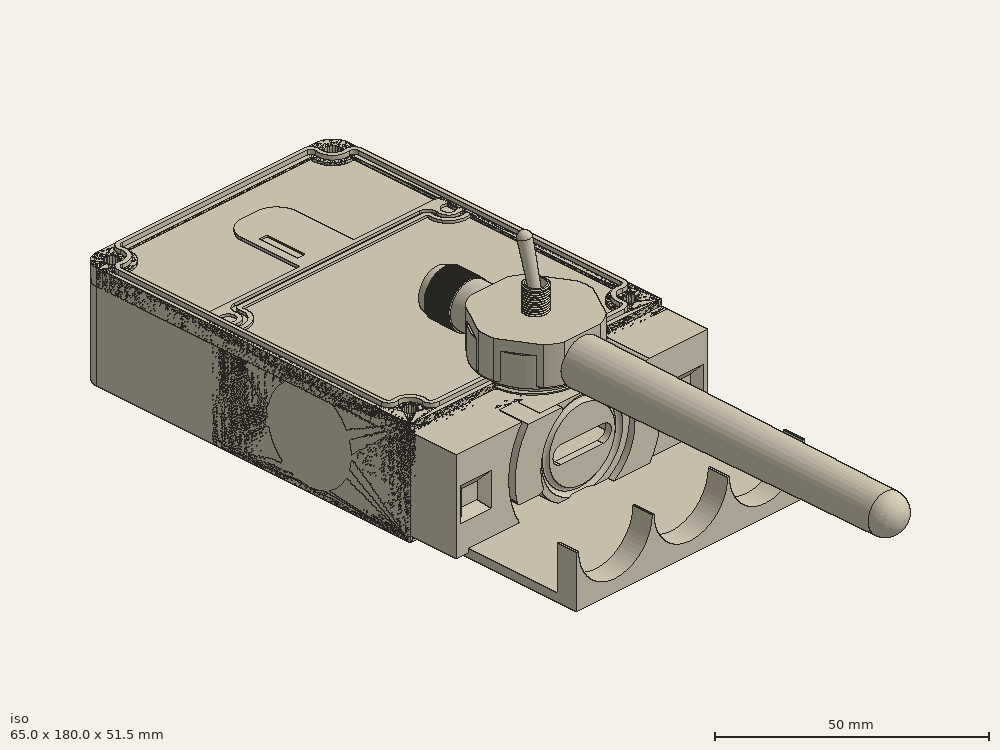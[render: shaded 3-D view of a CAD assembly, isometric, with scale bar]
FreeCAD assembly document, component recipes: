
FREECAD ASSEMBLY — COMPONENT RECIPES ("NomadShell_0.1")

This assembly document has 23 components, labeled P0..P22 below (a component is one placed body or linked part). 12 of them carry a construction recipe — the FreeCAD feature program that regenerates the part from scratch, quoted from this document or its linked companion documents; the rest are supplied as boundary geometry only. No exploded tour is included for this assembly.
NOTE — document 2 of 2 of this assembly tour. The two overview renders and the header above are repeated from document 1; the component sections below continue where the previous document stopped.
COMPONENT P12 — recipe-attached ("battery_top001", modeled in this document).
Construction recipe (the document's own serialized feature program — sketch geometry with constraints, then the solid features built on it; lengths are millimeters unless a unit is written):

FEATURE [PartDesign::SubShapeBinder] Binder005
  BindCopyOnChange = 0
  BindMode = 0
  ClaimChildren = false
  Context = -> Part009 [Body015.Binder005.]
  Fuse = false
  MakeFace = true
  OffsetFill = false
  OffsetIntersection = false
  OffsetJoinType = 0
  OffsetOpenResult = false
  PartialLoad = false
  Refine = true
  Relative = true
  Support = -> [Part002[Body002.Sketch007.]]
  _Version = 2
FEATURE [Sketcher::SketchObject] Sketch071  label="battery_holder"
  ArcFitTolerance = 1e-06
  AttachmentSupport = -> [XZ_Plane082]
  ExternalGeometry = -> [Binder005]
  ExternalTypes = [0,0,0,0,0,0,0,0,0,0,0]
  FullyConstrained = true
  MakeInternals = false
  MapMode = 5
  Placement = pos=(0,0,0) rot=(1,0,0;1.5708rad)
  sketch-geometry (3):
    g0: LineSegment StartX=-29.4 StartY=-12 StartZ=0 EndX=-29.4 EndY=-24.5 EndZ=0
    g1: LineSegment StartX=-29.4 StartY=-24.5 StartZ=0 EndX=29.5 EndY=-24.5 EndZ=0
    g2: LineSegment StartX=29.5 StartY=-24.5 StartZ=0 EndX=29.5 EndY=-12 EndZ=0
  constraints (8):
    c: Coincident(g-4,g0)
    c: Vertical(g0)
    c: Coincident(g0,g1)
    c: Horizontal(g1)
    c: Coincident(g1,g2)
    c: Coincident(g2,g-10)
    c: Parallel(g2,g-2)
    c: Distance(g-5,g1) = 3
FEATURE [PartDesign::Pad] Pad026  label="battery_holder001"
  Direction = (0,-1,2e-16)
  Length = 5
  Length2 = 10
  Placement = pos=(0,0,0) rot=(1,0,0;1.5708rad)
  Profile = -> Sketch071 [Edge2,Edge3,Vertex4,Edge4,Edge5,Edge6,Edge7,Edge8,Edge9,Edge10,Edge1]
  ReferenceAxis = -> Sketch071 [N_Axis]
  Refine = true
  Suppressed = false
  Type = 0
FEATURE [Sketcher::SketchObject] Sketch072
  ArcFitTolerance = 1e-06
  AttachmentSupport = -> [XZ_Plane082]
  ExternalGeometry = -> [Sketch071]
  ExternalTypes = [0]
  FullyConstrained = true
  MakeInternals = false
  MapMode = 5
  Placement = pos=(0,0,0) rot=(1,0,0;1.5708rad)
  sketch-geometry (3):
    g0: LineSegment StartX=-29.4 StartY=-24.5 StartZ=0 EndX=-29.4 EndY=-22.5 EndZ=0
    g1: LineSegment StartX=-29.4 StartY=-22.5 StartZ=0 EndX=29.5 EndY=-22.5 EndZ=0
    g2: LineSegment StartX=29.5 StartY=-22.5 StartZ=0 EndX=29.5 EndY=-24.5 EndZ=0
  constraints (8):
    c: Coincident(g0,g-3)
    c: Coincident(g0,g1)
    c: Horizontal(g1)
    c: Coincident(g1,g2)
    c: Coincident(g2,g-3)
    c: Parallel(g2,g-2)
    c: Parallel(g0,g-2)
    c: Distance(g0,g0) = 2
FEATURE [PartDesign::Pad] Pad027
  BaseFeature = -> Pad026
  Direction = (0,-1,2e-16)
  Length = 20
  Length2 = 10
  Placement = pos=(0,0,0) rot=(1,0,0;1.5708rad)
  Profile = -> Sketch072
  ReferenceAxis = -> Sketch072 [N_Axis]
  Refine = true
  Suppressed = false
  Type = 0
FEATURE [PartDesign::Mirrored] Mirrored
  BaseFeature = -> Pad027
  MirrorPlane = -> Pad027 [Face1]
  Originals = -> [Pad027]
  Placement = pos=(0,0,0) rot=(1,0,0;1.5708rad)
  Refine = true
  Suppressed = false
  TransformMode = 1
FEATURE [PartDesign::Body] Body015  label="Body"
  AllowCompound = false
  Group = -> [Binder005,Sketch071,Pad026,Sketch072,Pad027,Mirrored]
  Origin = -> Origin165
  Tip = -> Mirrored
COMPONENT P13 — recipe-attached ("gasket_main_body003", modeled in this document).
Construction recipe (the document's own serialized feature program — sketch geometry with constraints, then the solid features built on it; lengths are millimeters unless a unit is written):

FEATURE [PartDesign::SubShapeBinder] Binder
  BindCopyOnChange = 0
  BindMode = 0
  ClaimChildren = false
  Context = -> Body001 [Binder.]
  Fuse = false
  MakeFace = true
  OffsetFill = false
  OffsetIntersection = false
  OffsetJoinType = 0
  OffsetOpenResult = false
  PartialLoad = false
  Refine = true
  Relative = true
  Support = -> [Part[Body.Sketch.]]
  _Version = 2
FEATURE [Sketcher::SketchObject] Sketch027  label="center_line"
  ArcFitTolerance = 1e-06
  AttachmentSupport = -> [XY_Plane055]
  ExternalGeometry = -> [Binder]
  ExternalTypes = [0,0,0,0,0,0,0,0,0,0,0,0,0,0,0,0]
  FullyConstrained = true
  MakeInternals = false
  MapMode = 5
FEATURE [Sketcher::SketchObject] Sketch069  label="profile"
  ArcFitTolerance = 1e-06
  AttachmentSupport = -> [YZ_Plane055]
  ExternalGeometry = -> [Sketch027]
  ExternalTypes = [0]
  FullyConstrained = true
  MakeInternals = false
  MapMode = 5
  Placement = pos=(0,0,0) rot=(0.57735,0.57735,0.57735;2.0944rad)
  expr: Constraints[10] = VarSet.Base_gasket_width
  expr: Constraints[11] = VarSet.Base_gasket_height
  sketch-geometry (5):
    g0: LineSegment StartX=1 StartY=1 StartZ=0 EndX=1 EndY=-1 EndZ=0
    g1: LineSegment StartX=1 StartY=-1 StartZ=0 EndX=2 EndY=-1 EndZ=0
    g2: LineSegment StartX=2 StartY=-1 StartZ=0 EndX=2 EndY=1 EndZ=0
    g3: LineSegment StartX=2 StartY=1 StartZ=0 EndX=1 EndY=1 EndZ=0
    g4: GeomPoint [constr] X=1.5 Y=0 Z=0
  constraints (12):
    c: Coincident(g0,g1)
    c: Coincident(g1,g2)
    c: Coincident(g2,g3)
    c: Coincident(g3,g0)
    c: Vertical(g0)
    c: Vertical(g2)
    c: Horizontal(g1)
    c: Horizontal(g3)
    c: Symmetric(g2,g0,g4)
    c: Coincident(g4,g-3)
    c: Distance(g3,g3) = 1
    c: DistanceY(g0,g0) = 2
FEATURE [PartDesign::AdditivePipe] AdditivePipe
  AuxilleryCurvelinear = true
  AuxillerySpineTangent = false
  Binormal = (0,0,0)
  Mode = 0
  Placement = pos=(0,0,0) rot=(1,1,1;2.0944rad)
  Profile = -> Sketch069
  Refine = true
  Spine = -> Sketch027 [Edge1,Edge16,Edge15,Edge14,Edge13,Edge12,Edge11,Edge10,Edge9,Edge8,Edge7,Edge6,Edge5,Edge4,Edge3,Edge2]
  SpineTangent = false
  Suppressed = false
  Transformation = 0
  Transition = 0
FEATURE [PartDesign::Body] Body001  label="gasket_main_body001"
  AllowCompound = false
  Group = -> [Binder,Sketch027,Sketch069,AdditivePipe]
  Origin = -> Origin110
  Tip = -> AdditivePipe
COMPONENT P14 — recipe-attached ("gps_antenna002", modeled in this document).
Construction recipe (the document's own serialized feature program — sketch geometry with constraints, then the solid features built on it; lengths are millimeters unless a unit is written):

FEATURE [Sketcher::SketchObject] Sketch042
  ArcFitTolerance = 1e-06
  AttachmentSupport = -> [XY_Plane077]
  ExternalTypes = [0]
  FullyConstrained = true
  MakeInternals = false
  MapMode = 5
  expr: Constraints[10] = VarSet.Base_gps_antenna_width
  expr: Constraints[11] = VarSet.Base_gps_antenna_lenght
  sketch-geometry (15):
    g0: LineSegment StartX=-7.5 StartY=7.5 StartZ=0 EndX=-7.5 EndY=-7.5 EndZ=0
    g1: LineSegment StartX=-7.5 StartY=-7.5 StartZ=0 EndX=7.5 EndY=-7.5 EndZ=0
    g2: LineSegment StartX=7.5 StartY=-7.5 StartZ=0 EndX=7.5 EndY=7.5 EndZ=0
    g3: LineSegment StartX=7.5 StartY=7.5 StartZ=0 EndX=-7.5 EndY=7.5 EndZ=0
    g4: GeomPoint [constr] X=0 Y=0 Z=0
    g5: LineSegment StartX=-6.5 StartY=-6.5 StartZ=0 EndX=6.5 EndY=-6.5 EndZ=0
    g6: LineSegment StartX=6.5 StartY=-6.5 StartZ=0 EndX=6.5 EndY=6.5 EndZ=0
    g7: LineSegment StartX=6.5 StartY=6.5 StartZ=0 EndX=-6.5 EndY=6.5 EndZ=0
    g8: LineSegment StartX=-6.5 StartY=6.5 StartZ=0 EndX=-6.5 EndY=-6.5 EndZ=0
    g9: GeomPoint [constr] X=0 Y=0 Z=0
    g10: LineSegment StartX=-6 StartY=-6 StartZ=0 EndX=6 EndY=-6 EndZ=0
    g11: LineSegment StartX=6 StartY=-6 StartZ=0 EndX=6 EndY=6 EndZ=0
    g12: LineSegment StartX=6 StartY=6 StartZ=0 EndX=-6 EndY=6 EndZ=0
    g13: LineSegment StartX=-6 StartY=6 StartZ=0 EndX=-6 EndY=-6 EndZ=0
    g14: GeomPoint [constr] X=0 Y=0 Z=0
  constraints (36):
    c: Coincident(g0,g1)
    c: Coincident(g1,g2)
    c: Coincident(g2,g3)
    c: Coincident(g3,g0)
    c: Vertical(g0)
    c: Vertical(g2)
    c: Horizontal(g1)
    c: Horizontal(g3)
    c: Symmetric(g2,g0,g4)
    c: Coincident(g4,g-1)
    c: DistanceX(g0,g2) = 15
    c: DistanceY(g0,g0) = 15
    c: Coincident(g5,g6)
    c: Coincident(g6,g7)
    c: Coincident(g7,g8)
    c: Coincident(g8,g5)
    c: Horizontal(g5)
    c: Horizontal(g7)
    c: Vertical(g6)
    c: Vertical(g8)
    c: Symmetric(g7,g5,g9)
    c: Distance(g6,g8) = 13
    c: Distance(g5,g7) = 13
    c: Coincident(g9,g4)
    c: Coincident(g10,g11)
    c: Coincident(g11,g12)
    c: Coincident(g12,g13)
    c: Coincident(g13,g10)
    c: Horizontal(g10)
    c: Horizontal(g12)
    c: Vertical(g11)
    c: Vertical(g13)
    c: Symmetric(g12,g10,g14)
    c: Distance(g11,g13) = 12
    c: Distance(g10,g12) = 12
    c: Coincident(g14,g4)
FEATURE [PartDesign::Pad] Pad015
  Direction = (0,0,1)
  Length = 0.6
  Length2 = 10
  Profile = -> Sketch042 [Edge4,Edge3,Edge2,Edge1]
  ReferenceAxis = -> Sketch042 [N_Axis]
  Refine = true
  Suppressed = false
  Type = 0
FEATURE [PartDesign::Pad] Pad016
  BaseFeature = -> Pad015
  Direction = (0,0,1)
  Length = 5
  Length2 = 10
  Profile = -> Sketch042 [Edge5,Edge8,Edge7,Edge6]
  ReferenceAxis = -> Sketch042 [N_Axis]
  Refine = true
  Suppressed = false
  Type = 0
FEATURE [PartDesign::Pad] Pad017
  BaseFeature = -> Pad016
  Direction = (0,0,1)
  Length = 1.3
  Length2 = 10
  Profile = -> Sketch042 [Edge12,Edge9,Edge10,Edge11]
  ReferenceAxis = -> Sketch042 [N_Axis]
  Refine = true
  Reversed = true
  Suppressed = false
  Type = 0
FEATURE [Sketcher::SketchObject] Sketch044
  ArcFitTolerance = 1e-06
  ExternalTypes = [0]
  FullyConstrained = true
  MakeInternals = false
  MapMode = 5
  Placement = pos=(0,0,5) rot=(0,0,1;0rad)
  sketch-geometry (1):
    g0: Circle CenterX=0 CenterY=1.5 CenterZ=0 NormalX=0 NormalY=0 NormalZ=1 AngleXU=0 Radius=1
  constraints (3):
    c: PointOnObject(g0,g-2)
    c: Diameter(g0) = 2
    c: DistanceY(g-1,g0) = 1.5
FEATURE [PartDesign::Pad] Pad018
  BaseFeature = -> Pad017
  Direction = (0,0,1)
  Length = 1
  Length2 = 10
  Profile = -> Sketch044
  ReferenceAxis = -> Sketch044 [N_Axis]
  Refine = true
  Suppressed = false
  Type = 0
FEATURE [PartDesign::Chamfer] Chamfer
  Angle = 45
  Base = -> Pad018 [Edge21,Edge24,Edge26,Vertex18,Edge22]
  BaseFeature = -> Pad018
  ChamferType = 0
  FlipDirection = false
  Refine = true
  Size = 2
  Size2 = 1
  SupportTransform = false
  Suppressed = false
  UseAllEdges = false
FEATURE [Sketcher::SketchObject] Sketch045
  ArcFitTolerance = 1e-06
  AttachmentSupport = -> [Chamfer]
  ExternalTypes = [0]
  FullyConstrained = true
  MakeInternals = false
  MapMode = 5
  Placement = pos=(0,6,0) rot=(0,0.707107,0.707107;3.14159rad)
  sketch-geometry (1):
    g0: Circle CenterX=0 CenterY=-0.7 CenterZ=0 NormalX=0 NormalY=0 NormalZ=1 AngleXU=0 Radius=0.5
  constraints (3):
    c: PointOnObject(g0,g-2)
    c: Diameter(g0) = 1
    c: Distance(g0,g-1) = 0.7
FEATURE [PartDesign::Pad] Pad019
  BaseFeature = -> Chamfer
  Direction = (0,1,-2e-16)
  Length = 5
  Length2 = 10
  Profile = -> Sketch045
  ReferenceAxis = -> Sketch045 [N_Axis]
  Refine = true
  Suppressed = false
  Type = 0
FEATURE [PartDesign::Body] Body012  label="gps_antenna001"
  AllowCompound = false
  Group = -> [Sketch042,Pad015,Pad016,Pad017,Sketch044,Pad018,Chamfer,Sketch045,Pad019]
  Origin = -> Origin155
  Tip = -> Pad019
COMPONENT P15 — recipe-attached ("mainbody_cover002", modeled in this document).
Construction recipe (the document's own serialized feature program — sketch geometry with constraints, then the solid features built on it; lengths are millimeters unless a unit is written):

FEATURE [Sketcher::SketchObject] Sketch025
  ArcFitTolerance = 1e-06
  AttachmentSupport = -> [XY_Plane070]
  ExternalTypes = [0]
  FullyConstrained = true
  MakeInternals = false
  MapMode = 5
  expr: Constraints[7] = VarSet.base_width
  expr: Constraints[8] = VarSet.Base_base_lenght
  sketch-geometry (8):
    g0: LineSegment StartX=-32.5 StartY=51 StartZ=0 EndX=-32.5 EndY=0 EndZ=0
    g1: LineSegment StartX=-32.5 StartY=0 StartZ=0 EndX=32.5 EndY=0 EndZ=0
    g2: LineSegment StartX=32.5 StartY=0 StartZ=0 EndX=32.5 EndY=51 EndZ=0
    g3: LineSegment StartX=28.5 StartY=55 StartZ=0 EndX=-28.5 EndY=55 EndZ=0
    g4: ArcOfCircle CenterX=-28.5 CenterY=51 CenterZ=0 NormalX=0 NormalY=0 NormalZ=1 AngleXU=0 Radius=4 StartAngle=1.5708 EndAngle=3.14159
    g5: GeomPoint [constr] X=-32.5 Y=55 Z=0
    g6: ArcOfCircle CenterX=28.5 CenterY=51 CenterZ=0 NormalX=0 NormalY=0 NormalZ=1 AngleXU=0 Radius=4 StartAngle=4.17e-14 EndAngle=1.5708
    g7: GeomPoint [constr] X=32.5 Y=55 Z=0
  constraints (19):
    c: Coincident(g0,g1)
    c: Coincident(g1,g2)
    c: Vertical(g0)
    c: Vertical(g2)
    c: Horizontal(g1)
    c: PointOnObject(g1,g-1)
    c: Symmetric(g5,g7,g-2)
    c: DistanceX(g5,g7) = 65
    c: DistanceY(g1,g7) = 55
    c: PointOnObject(g5,g0)
    c: PointOnObject(g5,g3)
    c: Tangent(g0,g4) = -1.5708
    c: Tangent(g3,g4) = -1.5708
    c: PointOnObject(g7,g2)
    c: PointOnObject(g7,g3)
    c: Tangent(g2,g6) = -1.5708
    c: Tangent(g3,g6) = -1.5708
    c: Equal(g4,g6)
    c: Radius(g4) = 4
FEATURE [PartDesign::SubShapeBinder] Binder001
  BindCopyOnChange = 0
  BindMode = 0
  ClaimChildren = false
  Context = -> Body007 [Binder001.]
  Fuse = false
  MakeFace = true
  OffsetFill = false
  OffsetIntersection = false
  OffsetJoinType = 0
  OffsetOpenResult = false
  PartialLoad = false
  Refine = true
  Relative = true
  Support = -> [Part[Body.Sketch.]]
  _Version = 2
FEATURE [PartDesign::Pad] Pad011
  Direction = (0,0,1)
  Length = 5
  Length2 = 10
  Profile = -> Sketch025
  ReferenceAxis = -> Sketch025 [N_Axis]
  Refine = true
  Suppressed = false
  Type = 0
  expr: Length = VarSet.Base_lid_thickness
FEATURE [Sketcher::SketchObject] Sketch026
  ArcFitTolerance = 1e-06
  AttachmentSupport = -> [Pad011]
  ExternalGeometry = -> [Binder001]
  ExternalTypes = [0,0,0,0]
  FullyConstrained = false
  MakeInternals = false
  MapMode = 5
  Placement = pos=(0,0,5) rot=(0,0,1;0rad)
  sketch-geometry (4):
    g0: Circle CenterX=-28.5 CenterY=51 CenterZ=0 NormalX=0 NormalY=0 NormalZ=1 AngleXU=0 Radius=3.19333
    g1: Circle CenterX=28.5 CenterY=51 CenterZ=0 NormalX=0 NormalY=0 NormalZ=1 AngleXU=0 Radius=3.19333
    g2: Circle CenterX=28.5 CenterY=4 CenterZ=0 NormalX=0 NormalY=0 NormalZ=1 AngleXU=0 Radius=3.19333
    g3: Circle CenterX=-28.5 CenterY=4 CenterZ=0 NormalX=0 NormalY=0 NormalZ=1 AngleXU=0 Radius=3.19333
  constraints (7):
    c: Coincident(g0,g-3)
    c: Coincident(g1,g-4)
    c: Coincident(g2,g-5)
    c: Coincident(g3,g-6)
    c: Equal(g3,g2)
    c: Equal(g2,g1)
    c: Equal(g1,g0)
FEATURE [PartDesign::Hole] Hole
  BaseFeature = -> Pad011
  CustomThreadClearance = 0
  Depth = 25
  DepthType = 0
  Diameter = 3.4
  DrillForDepth = false
  DrillPoint = 1
  DrillPointAngle = 118
  HoleCutCountersinkAngle = 90
  HoleCutCustomValues = false
  HoleCutDepth = 0
  HoleCutDiameter = 6.7
  HoleCutType = 2
  ModelThread = false
  Profile = -> Sketch026
  Refine = true
  Suppressed = false
  Tapered = false
  TaperedAngle = 90
  ThreadClass = 0
  ThreadDepth = 25
  ThreadDepthType = 0
  ThreadDirection = 0
  ThreadFit = 0
  ThreadSize = 9
  ThreadType = 1
  Threaded = false
  UseCustomThreadClearance = false
FEATURE [Sketcher::SketchObject] Sketch034  label="gasket"
  ArcFitTolerance = 1e-06
  AttachmentSupport = -> [XY_Plane070]
  ExternalGeometry = -> [Binder001]
  ExternalTypes = [0,0,0,0,0,0,0,0,0,0,0,0,0,0,0,0,0]
  FullyConstrained = true
  MakeInternals = false
  MapMode = 5
FEATURE [Sketcher::SketchObject] Sketch035
  ArcFitTolerance = 1e-06
  AttachmentSupport = -> [YZ_Plane070]
  ExternalGeometry = -> [Sketch034]
  ExternalTypes = [0]
  FullyConstrained = true
  MakeInternals = false
  MapMode = 5
  Placement = pos=(0,0,0) rot=(0.57735,0.57735,0.57735;2.0944rad)
  expr: Constraints[10] = VarSet.Base_gasket_width
  expr: Constraints[11] = VarSet.Base_gasket_height
  sketch-geometry (5):
    g0: LineSegment StartX=1 StartY=1 StartZ=0 EndX=1 EndY=-1 EndZ=0
    g1: LineSegment StartX=1 StartY=-1 StartZ=0 EndX=2 EndY=-1 EndZ=0
    g2: LineSegment StartX=2 StartY=-1 StartZ=0 EndX=2 EndY=1 EndZ=0
    g3: LineSegment StartX=2 StartY=1 StartZ=0 EndX=1 EndY=1 EndZ=0
    g4: GeomPoint [constr] X=1.5 Y=0 Z=0
  constraints (12):
    c: Coincident(g0,g1)
    c: Coincident(g1,g2)
    c: Coincident(g2,g3)
    c: Coincident(g3,g0)
    c: Vertical(g0)
    c: Vertical(g2)
    c: Horizontal(g1)
    c: Horizontal(g3)
    c: Symmetric(g2,g0,g4)
    c: Coincident(g4,g-3)
    c: DistanceX(g0,g2) = 1
    c: DistanceY(g0,g0) = 2
FEATURE [PartDesign::SubtractivePipe] SubtractivePipe002
  AuxilleryCurvelinear = true
  AuxillerySpineTangent = false
  BaseFeature = -> Hole
  Binormal = (0,0,0)
  Mode = 0
  Profile = -> Sketch035
  Refine = true
  Spine = -> Sketch034 [Edge13,Edge14,Edge15,Edge16,Edge1,Edge2,Edge3,Edge4,Edge5,Edge6,Edge7,Edge8,Edge9,Edge10,Edge11,Edge12]
  SpineTangent = false
  Suppressed = false
  Transformation = 0
  Transition = 0
FEATURE [Sketcher::SketchObject] Sketch067  label="seses"
  ArcFitTolerance = 1e-06
  AttachmentSupport = -> [XY_Plane070]
  ExternalGeometry = -> [Binder001]
  ExternalTypes = [0,0,0,0,0,0,0,0]
  FullyConstrained = true
  MakeInternals = false
  MapMode = 5
FEATURE [PartDesign::Pocket] Pocket034
  BaseFeature = -> SubtractivePipe002
  Direction = (0,0,-1)
  Length = 0.6
  Length2 = 5
  Profile = -> Sketch067
  ReferenceAxis = -> Sketch067 [N_Axis]
  Refine = true
  Reversed = true
  Suppressed = false
  Type = 0
  expr: Length = 0.2 * VarSet.Base_case_thickness
FEATURE [PartDesign::Fillet] Fillet005
  Base = -> Pocket034 [Edge4,Edge7,Edge34,Edge35,Edge10,Edge36]
  BaseFeature = -> Pocket034
  Radius = 1
  Refine = true
  SupportTransform = false
  Suppressed = false
  UseAllEdges = false
FEATURE [PartDesign::Body] Body007  label="mainbody_cover001"
  AllowCompound = false
  Group = -> [Sketch025,Binder001,Pad011,Sketch026,Hole,Sketch034,Sketch035,SubtractivePipe002,Sketch067,Pocket034,Fillet005]
  Origin = -> Origin141
  Tip = -> Fillet005
COMPONENT P16 — geometry summary ("on_off_switch002"; no construction recipe available for this part):
  bounding box: 30.5 x 13.0 x 7.9 mm
  tessellated surface: 29,670 triangles
  volume: 1114 mm^3 (36% of its bounding box)
  symmetry: mirror-symmetric across its z mid-plane
COMPONENT P17 — recipe-attached ("oring002", modeled in this document).
Construction recipe (the document's own serialized feature program — sketch geometry with constraints, then the solid features built on it; lengths are millimeters unless a unit is written):

FEATURE [Sketcher::SketchObject] Sketch055
  ArcFitTolerance = 1e-06
  AttachmentSupport = -> [XY_Plane079]
  ExternalTypes = [0]
  FullyConstrained = false
  MakeInternals = false
  MapMode = 5
  expr: Constraints[0] = VarSet.Base_connector_oring_cross_section
  expr: Constraints[1] = (VarSet.Base_connector_oring_outside_diameter - VarSet.Base_connector_oring_cross_section) / 2
  expr: Constraints[4] = VarSet.Base_connector_oring_outside_diameter / 2
  sketch-geometry (2):
    g0: Circle CenterX=9.5 CenterY=0 CenterZ=0 NormalX=0 NormalY=0 NormalZ=1 AngleXU=0 Radius=1
    g1: LineSegment [constr] StartX=0 StartY=0 StartZ=0 EndX=10.5 EndY=0 EndZ=0
  constraints (5):
    c: Diameter(g0) = 2
    c: DistanceX(g-1,g0) = 9.5
    c: Coincident(g1,g-1)
    c: PointOnObject(g1,g-1)
    c: DistanceX(g1,g1) = 10.5
FEATURE [PartDesign::Revolution] Revolution002
  Angle = 360
  Angle2 = 60
  Axis = (0,1,0)
  Base = (0,0,0)
  Profile = -> Sketch055
  ReferenceAxis = -> Sketch055 [V_Axis]
  Refine = true
  Reversed = true
  Suppressed = false
  Type = 0
FEATURE [PartDesign::Body] Body013  label="oring001"
  AllowCompound = false
  Group = -> [Sketch055,Revolution002]
  Origin = -> Origin159
  Tip = -> Revolution002
COMPONENT P18 — geometry summary ("switch_cover001"; no construction recipe available for this part):
  bounding box: 17.0 x 10.9 x 9.7 mm
  tessellated surface: 23,872 triangles
  volume: 364 mm^3 (20% of its bounding box)
  symmetry: 6-fold rotationally symmetric about the y axis; mirror-symmetric across its x mid-plane
COMPONENT P19 — geometry summary ("usb_c_male001"; no construction recipe available for this part):
  bounding box: 38.4 x 11.8 x 6.9 mm
  tessellated surface: 6,336 triangles
  volume: 1915 mm^3 (61% of its bounding box)
  symmetry: 2-fold rotationally symmetric about the x axis; mirror-symmetric across its z mid-plane
COMPONENT P20 — recipe-attached ("usb_cover_base001", modeled in this document).
Construction recipe (the document's own serialized feature program — sketch geometry with constraints, then the solid features built on it; lengths are millimeters unless a unit is written):

FEATURE [Sketcher::SketchObject] Sketch008  label="main_usb_cover"
  ArcFitTolerance = 1e-06
  AttachmentSupport = -> [XZ_Plane063]
  ExternalTypes = [0]
  FullyConstrained = true
  MakeInternals = false
  MapMode = 5
  Placement = pos=(0,0,0) rot=(1,0,0;1.5708rad)
  expr: Constraints[12] = VarSet.Base_case_thickness / 2
  expr: Constraints[14] = VarSet.Base_usb_cover_main_diameter * 1.2 / 2
  expr: Constraints[15] = VarSet.Base_usb_cover_main_diameter / 2
  sketch-geometry (6):
    g0: LineSegment StartX=-9 StartY=0 StartZ=0 EndX=-10.8 EndY=0 EndZ=0
    g1: LineSegment StartX=-10.8 StartY=0 StartZ=0 EndX=-10.8 EndY=1.5 EndZ=0
    g2: LineSegment StartX=-10.8 StartY=1.5 StartZ=0 EndX=-10.4 EndY=1.5 EndZ=0
    g3: LineSegment StartX=-10.4 StartY=1.5 StartZ=0 EndX=-10.4 EndY=7.5 EndZ=0
    g4: LineSegment StartX=-10.4 StartY=7.5 StartZ=0 EndX=-9 EndY=7.5 EndZ=0
    g5: LineSegment StartX=-9 StartY=7.5 StartZ=0 EndX=-9 EndY=0 EndZ=0
  constraints (18):
    c: PointOnObject(g0,g-1)
    c: PointOnObject(g0,g-1)
    c: Coincident(g0,g1)
    c: Coincident(g1,g2)
    c: Horizontal(g2)
    c: Coincident(g2,g3)
    c: Coincident(g3,g4)
    c: Coincident(g4,g5)
    c: Coincident(g5,g0)
    c: Parallel(g5,g-2)
    c: Parallel(g4,g-1)
    c: Parallel(g1,g-2)
    c: DistanceY(g0,g1) = 1.5
    c: Parallel(g3,g5)
    c: DistanceX(g0,g-1) = 10.8
    c: DistanceX(g0,g-1) = 9
    c: DistanceY(g2,g3) = 6
    c: Distance(g4,g4) = 1.4
FEATURE [PartDesign::Revolution] Revolution
  Angle = 360
  Angle2 = 60
  Axis = (0,2e-16,1)
  Base = (0,0,0)
  Placement = pos=(0,0,0) rot=(1,0,0;1.5708rad)
  Profile = -> Sketch008
  ReferenceAxis = -> Sketch008 [V_Axis]
  Refine = true
  Suppressed = false
  Type = 0
FEATURE [PartDesign::Boolean] Boolean
  BaseFeature = -> Revolution
  Group = -> [ScrewDie]
  Refine = true
  Suppressed = false
  Type = 1
  UsePlacement = true
FEATURE [PartDesign::Body] Body003  label="usb_cover_base002"
  AllowCompound = false
  Group = -> [Sketch008,Revolution,Boolean]
  Origin = -> Origin126
  Tip = -> Boolean
COMPONENT P21 — recipe-attached ("usb_screw001", modeled in this document).
Construction recipe (the document's own serialized feature program — sketch geometry with constraints, then the solid features built on it; lengths are millimeters unless a unit is written):

FEATURE [Sketcher::SketchObject] Sketch009  label="main_screw"
  ArcFitTolerance = 1e-06
  AttachmentSupport = -> [XZ_Plane064]
  ExternalTypes = [0]
  FullyConstrained = true
  MakeInternals = false
  MapMode = 5
  Placement = pos=(0,0,0) rot=(1,0,0;1.5708rad)
  expr: Constraints[15] = VarSet.Base_usb_cover_main_diameter / 2
  sketch-geometry (6):
    g0: LineSegment StartX=0 StartY=9 StartZ=0 EndX=0 EndY=11 EndZ=0
    g1: LineSegment StartX=0 StartY=11 StartZ=0 EndX=-13 EndY=11 EndZ=0
    g2: LineSegment StartX=-13 StartY=11 StartZ=0 EndX=-13 EndY=2 EndZ=0
    g3: LineSegment StartX=-13 StartY=2 StartZ=0 EndX=-9 EndY=2 EndZ=0
    g4: LineSegment StartX=-9 StartY=2 StartZ=0 EndX=-9 EndY=9 EndZ=0
    g5: LineSegment StartX=-9 StartY=9 StartZ=0 EndX=0 EndY=9 EndZ=0
  constraints (18):
    c: PointOnObject(g0,g-2)
    c: PointOnObject(g0,g-2)
    c: Coincident(g0,g1)
    c: Horizontal(g1)
    c: Coincident(g1,g2)
    c: Vertical(g2)
    c: Coincident(g2,g3)
    c: Horizontal(g3)
    c: Coincident(g3,g4)
    c: Vertical(g4)
    c: Coincident(g4,g5)
    c: Coincident(g5,g0)
    c: Horizontal(g5)
    c: Distance(g0,g0) = 2
    c: DistanceX(g1,g4) = 4
    c: DistanceX(g4,g0) = 9
    c: DistanceY(g2,g2) = 9
    c: DistanceY(g-1,g0) = 9
FEATURE [PartDesign::Revolution] Revolution001
  Angle = 360
  Angle2 = 60
  Axis = (0,2e-16,1)
  Base = (0,0,0)
  Placement = pos=(0,0,0) rot=(1,0,0;1.5708rad)
  Profile = -> Sketch009
  ReferenceAxis = -> Sketch009 [V_Axis]
  Refine = true
  Suppressed = false
  Type = 0
FEATURE [Sketcher::SketchObject] Sketch010  label="cutout"
  ArcFitTolerance = 1e-06
  AttachmentSupport = -> [XY_Plane064]
  ExternalGeometry = -> [Revolution001]
  ExternalTypes = [0]
  FullyConstrained = true
  MakeInternals = false
  MapMode = 5
  sketch-geometry (7):
    g0: LineSegment StartX=14 StartY=0 StartZ=0 EndX=7 EndY=12.1244 EndZ=0
    g1: LineSegment StartX=7 StartY=12.1244 StartZ=0 EndX=-7 EndY=12.1244 EndZ=0
    g2: LineSegment StartX=-7 StartY=12.1244 StartZ=0 EndX=-14 EndY=-2.1849e-12 EndZ=0
    g3: LineSegment StartX=-14 StartY=-2.1849e-12 StartZ=0 EndX=-7 EndY=-12.1244 EndZ=0
    g4: LineSegment StartX=-7 StartY=-12.1244 StartZ=0 EndX=7 EndY=-12.1244 EndZ=0
    g5: LineSegment StartX=7 StartY=-12.1244 StartZ=0 EndX=14 EndY=0 EndZ=0
    g6: Circle [constr] CenterX=0 CenterY=0 CenterZ=0 NormalX=0 NormalY=0 NormalZ=1 AngleXU=0 Radius=14
  constraints (16):
    c: Coincident(g0,g1)
    c: Coincident(g1,g2)
    c: Coincident(g2,g3)
    c: Coincident(g3,g4)
    c: Coincident(g4,g5)
    c: Coincident(g5,g0)
    c: Equal(g0, g1-g5) x5
    c: PointOnObject(g0,g6)
    c: PointOnObject(g1,g6)
    c: PointOnObject(g2,g6)
    c: PointOnObject(g3,g6)
    c: PointOnObject(g4,g6)
    c: PointOnObject(g5,g6)
    c: Coincident(g6,g-1)
    c: PointOnObject(g5,g-1)
    c: Diameter(g6) = 28
FEATURE [PartDesign::Pocket] Pocket011
  BaseFeature = -> Revolution001
  Direction = (0,0,-1)
  Length = 5
  Length2 = 5
  Placement = pos=(0,0,0) rot=(1,0,0;1.5708rad)
  Profile = -> Sketch010
  ReferenceAxis = -> Sketch010 [N_Axis]
  Refine = true
  Reversed = true
  Suppressed = false
  Type = 1
FEATURE [PartDesign::Boolean] Boolean001
  BaseFeature = -> Pocket011
  Group = -> [ScrewTap]
  Refine = true
  Suppressed = false
  Type = 1
  UsePlacement = true
FEATURE [PartDesign::Body] Body004  label="usb_screw002"
  AllowCompound = false
  Group = -> [Sketch009,Revolution001,Sketch010,Pocket011,Boolean001]
  Origin = -> Origin129
  Tip = -> Boolean001
COMPONENT P22 — recipe-attached ("usb_screw_gasket002", modeled in this document).
Construction recipe (the document's own serialized feature program — sketch geometry with constraints, then the solid features built on it; lengths are millimeters unless a unit is written):

FEATURE [Sketcher::SketchObject] Sketch073
  ArcFitTolerance = 1e-06
  AttachmentSupport = -> [XY_Plane084]
  ExternalTypes = [0]
  FullyConstrained = true
  MakeInternals = false
  MapMode = 5
  sketch-geometry (1):
    g0: Circle CenterX=0 CenterY=0 CenterZ=0 NormalX=0 NormalY=0 NormalZ=1 AngleXU=0 Radius=9.5
  constraints (2):
    c: Coincident(g0,g-1)
    c: Diameter(g0) = 19
FEATURE [PartDesign::Pad] Pad028
  Direction = (0,0,1)
  Length = 1
  Length2 = 10
  Profile = -> Sketch073
  ReferenceAxis = -> Sketch073 [N_Axis]
  Refine = true
  Suppressed = false
  Type = 0
FEATURE [PartDesign::Body] Body016  label="usb_screw_gasket001"
  AllowCompound = false
  Group = -> [Sketch073,Pad028]
  Origin = -> Origin169
  Tip = -> Pad028
PROVENANCE & LICENSES
A FreeCAD (.FCStd) document from a public repository crawl; recipes are the document's own serialized feature recipes (and, for linked parts, companion documents' recipes).
License: mit.
